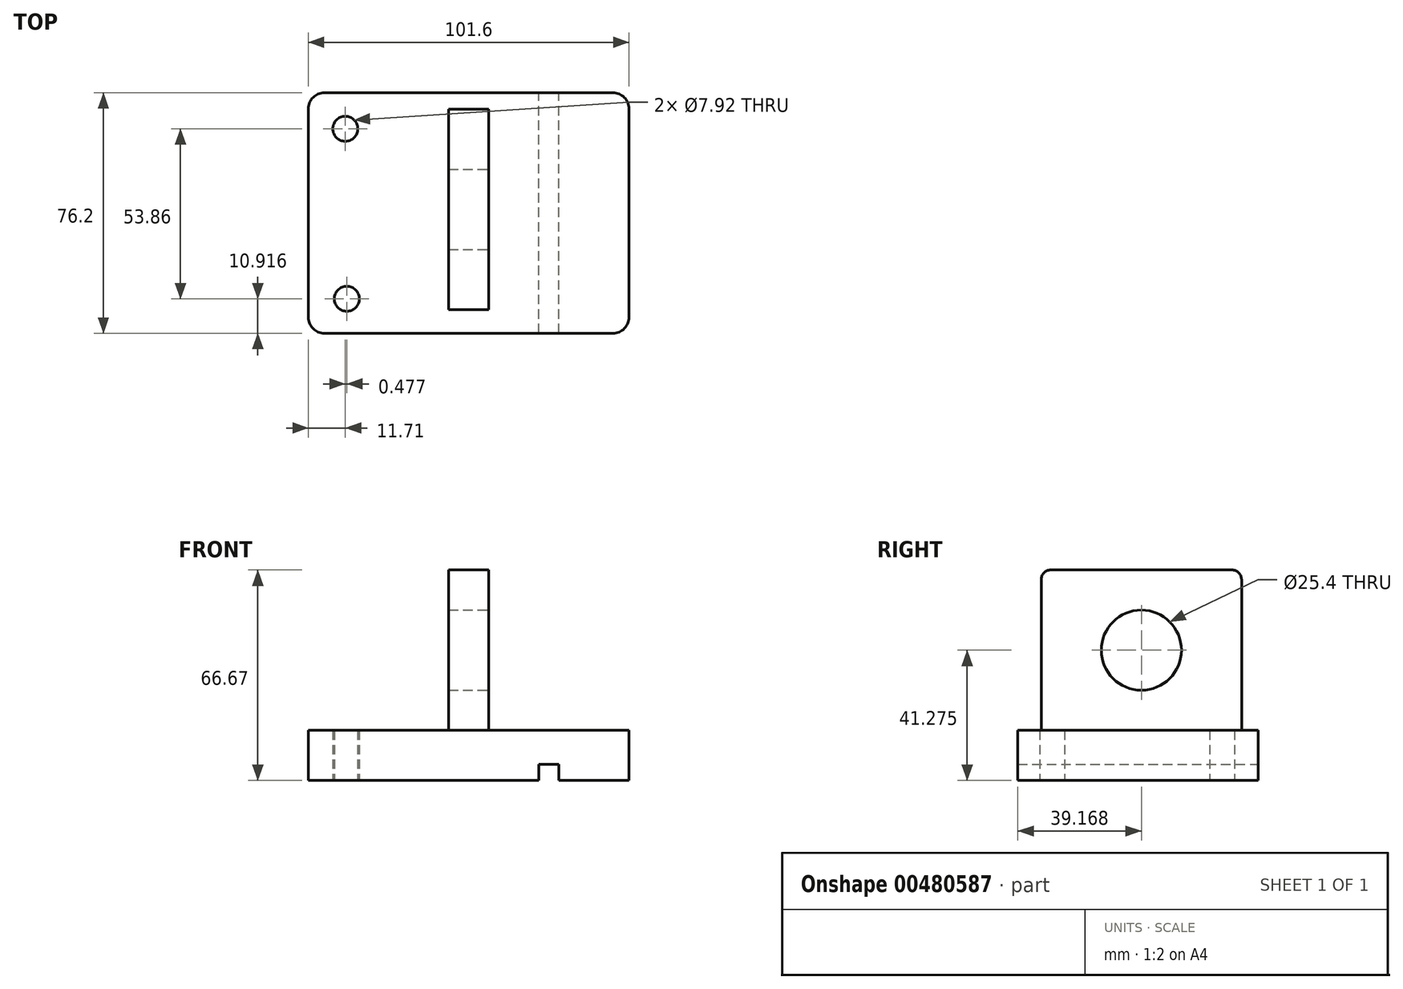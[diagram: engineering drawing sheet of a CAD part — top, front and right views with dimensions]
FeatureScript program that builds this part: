
annotation { "Feature Type Name" : "Feature", "Feature Type Description" : "" }
export const myFeature = defineFeature(function(context is Context, id is Id, definition is map)
    precondition{}
    {
        {
            var Q0;
            Q0=qCreatedBy(makeId("Top.planeOp"),FACE);
            var sketch = newSketch(context, id + "F0", { "sketchPlane" : qUnion([Q0])});
            skLineSegment(sketch, "E0.bottom", {"start": v(-52.06, 50.5) * mm, "end": v(49.54, 50.5) * mm});
            skLineSegment(sketch, "E0.top", {"start": v(-52.06, -25.7) * mm, "end": v(49.54, -25.7) * mm});
            skLineSegment(sketch, "E0.left", {"start": v(-52.06, 50.5) * mm, "end": v(-52.06, -25.7) * mm});
            skLineSegment(sketch, "E0.right", {"start": v(49.54, 50.5) * mm, "end": v(49.54, -25.7) * mm});
            skCircle(sketch, "E1", {"center": v(-40.35, 39.07) * mm, "radius": 3.96 * mm});
            skCircle(sketch, "E2", {"center": v(-39.87, -14.8) * mm, "radius": 3.96 * mm});
            skLineSegment(sketch, "E3.bottom", {"start": v(-7.6, 45.2) * mm, "end": v(5.1, 45.2) * mm});
            skLineSegment(sketch, "E3.top", {"start": v(-7.6, -18.3) * mm, "end": v(5.1, -18.3) * mm});
            skLineSegment(sketch, "E3.left", {"start": v(-7.6, 45.2) * mm, "end": v(-7.6, -18.3) * mm});
            skLineSegment(sketch, "E3.right", {"start": v(5.1, 45.2) * mm, "end": v(5.1, -18.3) * mm});
            skLineSegment(sketch, "E4", {"start": v(-1.26, -18.3) * mm, "end": v(-1.26, 45.2) * mm, "construction": true});
            skSolve(sketch);
        }
        {
            var Q0;
            Q0=makeQuery(id+"F0.imprint","IMPRINT",FACE,{"disambiguationData":[TD([[makeQuery(id+"F0.imprint","IMPRINT",EDGE,{"derivedFrom":sQuery(id+"F0.wireOp",EDGE,"E3.bottom")}),-1.0]])]});
            extrude(context, id + "F1", {"entities" : qUnion([Q0]), "depth" : 66.67 * mm});
        }
        {
            var Q0;
            Q0 = qSketchRegion(id + "F0", true);
            extrude(context, id + "F2", {"entities" : qUnion([Q0]), "operationType" : NewBodyOperationType.ADD, "depth" : 15.88 * mm});
        }
        {
            var Q0;
            Q0=makeQuery(id+"F1.opExtrude","CAP_EDGE",EDGE,{"disambiguationData":[OSD([sQuery(id+"F0.wireOp",EDGE,"E3.top")])],"isStart":false});
            var Q1;
            Q1=makeQuery(id+"F1.opExtrude","CAP_EDGE",EDGE,{"disambiguationData":[OSD([sQuery(id+"F0.wireOp",EDGE,"E3.bottom")])],"isStart":false});
            var Q2;
            Q2=makeQuery(id+"F2.opExtrude","CAP_EDGE",EDGE,{"disambiguationData":[OSD([sQuery(id+"F0.wireOp",EDGE,"E3.top")])],"isStart":false});
            var Q3;
            Q3=makeQuery(id+"F2.opExtrude","CAP_EDGE",EDGE,{"disambiguationData":[OSD([sQuery(id+"F0.wireOp",EDGE,"E3.bottom")])],"isStart":false});
            fillet(context, id + "F3", {"entities" : qUnion([Q0, Q1, Q2, Q3]), "radius" : 3.05 * mm, "tangentPropagation" : true, "allowEdgeOverflow" : false});
        }
        {
            var Q0;
            Q0=makeQuery(id+"F2.opExtrude","SWEPT_EDGE",EDGE,{"disambiguationData":[OSD([sQuery(id+"F0.wireOp",EDGE,"E0.top"),sQuery(id+"F0.wireOp",EDGE,"E0.left")])]});
            var Q1;
            Q1=makeQuery(id+"F2.opExtrude","SWEPT_EDGE",EDGE,{"disambiguationData":[OSD([sQuery(id+"F0.wireOp",EDGE,"E0.top"),sQuery(id+"F0.wireOp",EDGE,"E0.right")])]});
            var Q2;
            Q2=makeQuery(id+"F2.opExtrude","SWEPT_EDGE",EDGE,{"disambiguationData":[OSD([sQuery(id+"F0.wireOp",EDGE,"E0.bottom"),sQuery(id+"F0.wireOp",EDGE,"E0.right")])]});
            var Q3;
            Q3=makeQuery(id+"F2.opExtrude","SWEPT_EDGE",EDGE,{"disambiguationData":[OSD([sQuery(id+"F0.wireOp",EDGE,"E0.bottom"),sQuery(id+"F0.wireOp",EDGE,"E0.left")])]});
            fillet(context, id + "F4", {"entities" : qUnion([Q0, Q1, Q2, Q3]), "radius" : 5.08 * mm, "tangentPropagation" : true, "allowEdgeOverflow" : false});
        }
        {
            var Q0;
            Q0=makeQuery(id+"F1.opExtrude","SWEPT_FACE",FACE,{"disambiguationData":[OSD([sQuery(id+"F0.wireOp",EDGE,"E3.right")])]});
            var sketch = newSketch(context, id + "F5", { "sketchPlane" : qUnion([Q0])});
            skCircle(sketch, "E5", {"center": v(13.46, 41.28) * mm, "radius": 12.7 * mm});
            skSolve(sketch);
        }
        {
            var Q0;
            {var subQ0=sQuery(id+"F0.wireOp",EDGE,"E3.right");var subQ1=sQuery(id+"F0.wireOp",EDGE,"E3.left");var subQ2=sQuery(id+"F0.wireOp",EDGE,"E3.top");var subQ3=sQuery(id+"F0.wireOp",EDGE,"E3.bottom");Q0=makeQuery(id+"F2.boolean.opBoolean","MERGE",FACE,{"derivedFrom":[makeQuery(id+"F1.opExtrude","CAP_FACE",FACE,{"disambiguationData":[OSD([subQ3,subQ2,subQ1,subQ0])],"isStart":true}),makeQuery(id+"F2.opExtrude","CAP_FACE",FACE,{"disambiguationData":[OSD([sQuery(id+"F0.wireOp",EDGE,"E0.bottom"),sQuery(id+"F0.wireOp",EDGE,"E0.top"),sQuery(id+"F0.wireOp",EDGE,"E0.left"),sQuery(id+"F0.wireOp",EDGE,"E0.right"),sQuery(id+"F0.wireOp",EDGE,"E1"),sQuery(id+"F0.wireOp",EDGE,"E2"),subQ3,subQ2,subQ1,subQ0])],"isStart":true})]});}
            var sketch = newSketch(context, id + "F6", { "sketchPlane" : qUnion([Q0])});
            skLineSegment(sketch, "E6.bottom", {"start": v(20.97, 25.7) * mm, "end": v(27.32, 25.7) * mm});
            skLineSegment(sketch, "E6.top", {"start": v(20.97, -50.5) * mm, "end": v(27.32, -50.5) * mm});
            skLineSegment(sketch, "E6.left", {"start": v(20.97, 25.7) * mm, "end": v(20.97, -50.5) * mm});
            skLineSegment(sketch, "E6.right", {"start": v(27.32, 25.7) * mm, "end": v(27.32, -50.5) * mm});
            skSolve(sketch);
        }
        {
            var Q0;
            Q0=makeQuery(id+"F6.imprint","IMPRINT",FACE,{"disambiguationData":[TD([[makeQuery(id+"F6.imprint","IMPRINT",EDGE,{"derivedFrom":sQuery(id+"F6.wireOp",EDGE,"E6.bottom")}),-1.0]])]});
            extrude(context, id + "F7", {"entities" : qUnion([Q0]), "operationType" : NewBodyOperationType.REMOVE, "oppositeDirection" : true, "depth" : 5.08 * mm});
        }
        {
            var Q0;
            Q0=makeQuery(id+"F5.imprint","IMPRINT",FACE,{"disambiguationData":[TD([[makeQuery(id+"F5.imprint","IMPRINT",EDGE,{"derivedFrom":sQuery(id+"F5.wireOp",EDGE,"E5")}),1.0]])]});
            extrude(context, id + "F8", {"entities" : qUnion([Q0]), "operationType" : NewBodyOperationType.REMOVE, "oppositeDirection" : true, "depth" : 37.6 * mm});
        }
    });
